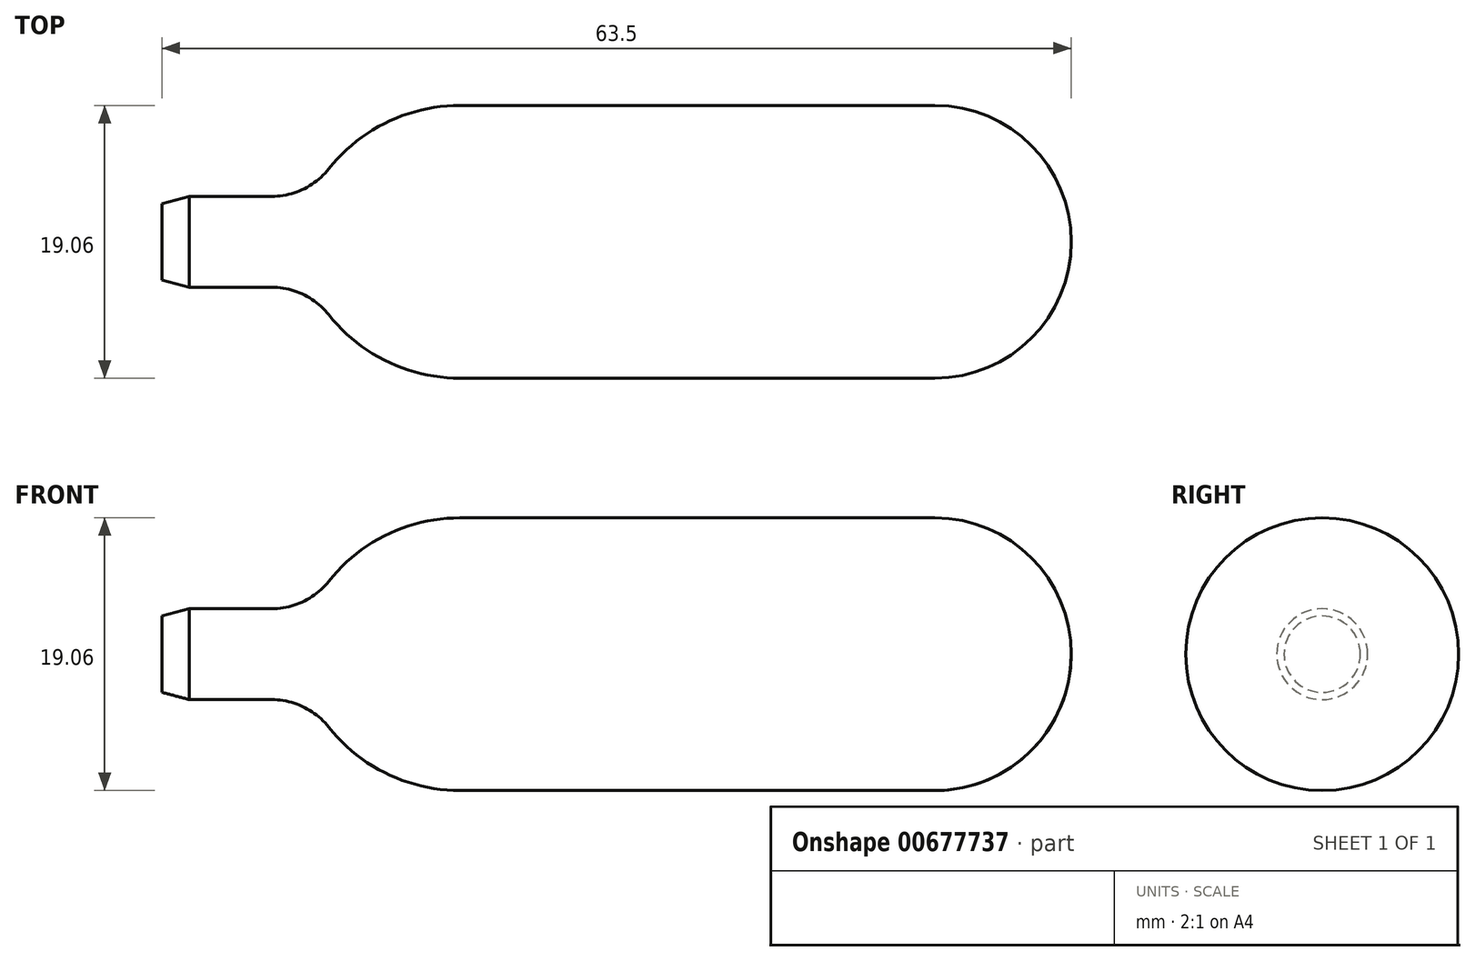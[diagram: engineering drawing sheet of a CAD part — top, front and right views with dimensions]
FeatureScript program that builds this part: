
annotation { "Feature Type Name" : "Feature", "Feature Type Description" : "" }
export const myFeature = defineFeature(function(context is Context, id is Id, definition is map)
    precondition{}
    {
        {
            var Q0;
            Q0=qCreatedBy(makeId("Front.planeOp"),FACE);
            var sketch = newSketch(context, id + "F0", { "sketchPlane" : qUnion([Q0])});
            skLineSegment(sketch, "E0", {"start": v(0, 0) * mm, "end": v(0, 3.18) * mm});
            skLineSegment(sketch, "E1", {"start": v(20.8, 9.53) * mm, "end": v(53.97, 9.53) * mm});
            skLineSegment(sketch, "E2", {"start": v(63.5, 0) * mm, "end": v(0, 0) * mm});
            skArc(sketch, "E3", {"start": v(63.5, 0) * mm, "mid": v(60.71, 6.74) * mm, "end": v(53.97, 9.53) * mm});
            skArc(sketch, "E4", {"start": v(20.8, 9.53) * mm, "mid": v(14.71, 7.81) * mm, "end": v(10.4, 3.18) * mm});
            skLineSegment(sketch, "E5", {"start": v(0, 3.18) * mm, "end": v(10.4, 3.17) * mm});
            skLineSegment(sketch, "E6", {"start": v(63.5, 0) * mm, "end": v(63.5, 14.27) * mm, "construction": true});
            skSolve(sketch);
        }
        {
            var Q0;
            {var subQ4=sQuery(id+"F0.wireOp",EDGE,"E0");Q0=makeQuery(id+"F0.imprint","IMPRINT",FACE,{"disambiguationData":[TD([[makeQuery(id+"F0.imprint","IMPRINT",EDGE,{"derivedFrom":subQ4}),-1.0]])]});}
            var Q1;
            Q1=sQuery(id+"F0.wireOp",EDGE,"E2");
            revolve(context, id + "F1", {"entities" : qUnion([Q0]), "axis" : qUnion([Q1]), "revolveType" : RevolveType.FULL});
        }
        {
            var Q0;
            Q0=makeQuery(id+"F1.opRevolve","SWEPT_EDGE",EDGE,{"disambiguationData":[OSD([sQuery(id+"F0.wireOp",EDGE,"E4"),sQuery(id+"F0.wireOp",EDGE,"E5")])]});
            fillet(context, id + "F2", {"entities" : qUnion([Q0]), "radius" : 5.08 * mm, "tangentPropagation" : true, "allowEdgeOverflow" : false});
        }
        {
            var Q0;
            Q0=makeQuery(id+"F1.opRevolve","SWEPT_EDGE",EDGE,{"disambiguationData":[OSD([sQuery(id+"F0.wireOp",EDGE,"E0"),sQuery(id+"F0.wireOp",EDGE,"E5")])]});
            chamfer(context, id + "F3", {"entities" : qUnion([Q0]), "chamferType" : ChamferType.OFFSET_ANGLE, "width" : 1.9 * mm, "oppositeDirection" : false, "angle" : 15 * degree, "tangentPropagation" : true});
        }
    });
